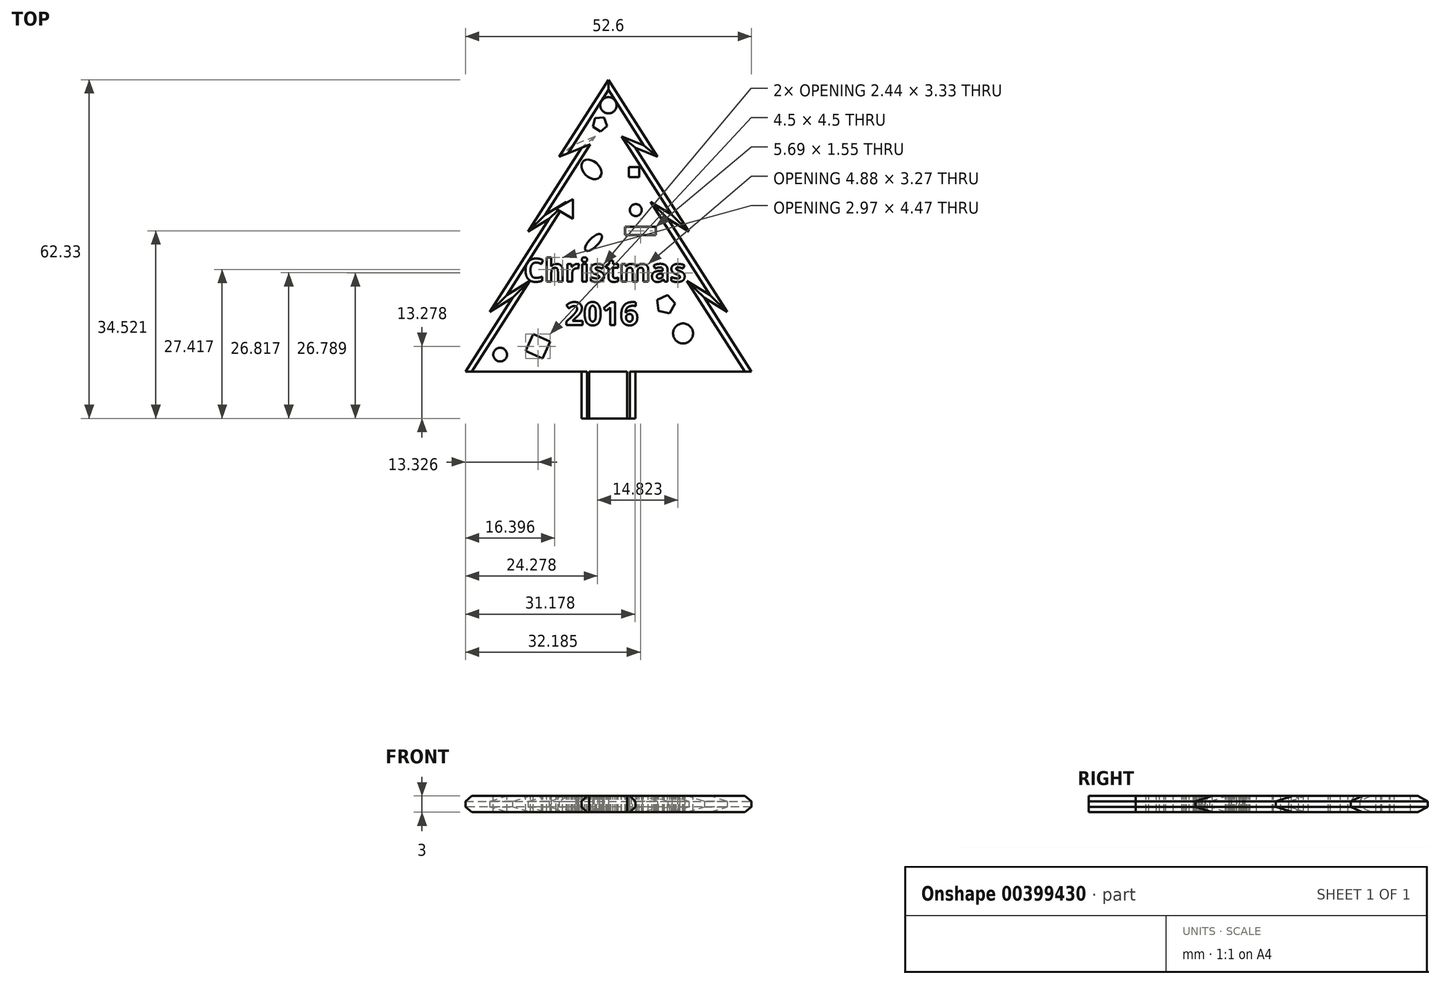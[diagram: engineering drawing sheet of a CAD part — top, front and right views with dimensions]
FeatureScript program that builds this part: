
annotation { "Feature Type Name" : "Feature", "Feature Type Description" : "" }
export const myFeature = defineFeature(function(context is Context, id is Id, definition is map)
    precondition{}
    {
        {
            var Q0;
            Q0=qCreatedBy(makeId("Top.planeOp"),FACE);
            var sketch = newSketch(context, id + "F0", { "sketchPlane" : qUnion([Q0])});
            skLineSegment(sketch, "E0", {"start": v(0, 62.33) * mm, "end": v(-9.05, 48.15) * mm});
            skLineSegment(sketch, "E1", {"start": v(-9.05, 48.15) * mm, "end": v(-4.95, 49.83) * mm});
            skLineSegment(sketch, "E2", {"start": v(-4.95, 49.83) * mm, "end": v(-14.78, 34.42) * mm});
            skLineSegment(sketch, "E3", {"start": v(-14.78, 34.42) * mm, "end": v(-10.92, 36.76) * mm});
            skLineSegment(sketch, "E4", {"start": v(-10.92, 36.76) * mm, "end": v(-21.87, 19.6) * mm});
            skLineSegment(sketch, "E5", {"start": v(-21.87, 19.6) * mm, "end": v(-17.63, 22.2) * mm});
            skLineSegment(sketch, "E6", {"start": v(-17.63, 22.2) * mm, "end": v(-26.3, 8.63) * mm});
            skLineSegment(sketch, "E7", {"start": v(-26.3, 8.63) * mm, "end": v(-4.95, 8.63) * mm});
            skLineSegment(sketch, "E8", {"start": v(-4.95, 8.63) * mm, "end": v(-4.95, 0) * mm});
            skLineSegment(sketch, "E9", {"start": v(-4.95, 0) * mm, "end": v(0, 0) * mm});
            skLineSegment(sketch, "E10.MirrorCS", {"start": v(0, 62.33) * mm, "end": v(9.05, 48.15) * mm});
            skLineSegment(sketch, "E11.MirrorCS", {"start": v(9.05, 48.15) * mm, "end": v(4.95, 49.83) * mm});
            skLineSegment(sketch, "E12.MirrorCS", {"start": v(4.95, 49.83) * mm, "end": v(14.78, 34.42) * mm});
            skLineSegment(sketch, "E13.MirrorCS", {"start": v(14.78, 34.42) * mm, "end": v(10.92, 36.76) * mm});
            skLineSegment(sketch, "E14.MirrorCS", {"start": v(10.92, 36.76) * mm, "end": v(21.87, 19.6) * mm});
            skLineSegment(sketch, "E15.MirrorCS", {"start": v(21.87, 19.6) * mm, "end": v(17.63, 22.2) * mm});
            skLineSegment(sketch, "E16.MirrorCS", {"start": v(17.63, 22.2) * mm, "end": v(26.3, 8.63) * mm});
            skLineSegment(sketch, "E17.MirrorCS", {"start": v(26.3, 8.63) * mm, "end": v(4.95, 8.63) * mm});
            skLineSegment(sketch, "E18.MirrorCS", {"start": v(4.95, 8.63) * mm, "end": v(4.95, 0) * mm});
            skLineSegment(sketch, "E19.MirrorCS", {"start": v(4.95, 0) * mm, "end": v(0, 0) * mm});
            skSolve(sketch);
        }
        {
            var Q0;
            Q0=makeQuery(id+"F0.imprint","IMPRINT",FACE,{"disambiguationData":[TD([[makeQuery(id+"F0.imprint","IMPRINT",EDGE,{"derivedFrom":sQuery(id+"F0.wireOp",EDGE,"E0")}),1.0]])]});
            extrude(context, id + "F1", {"entities" : qUnion([Q0]), "depth" : 3 * mm});
        }
        {
            var Q0;
            Q0=makeQuery(id+"F1.opExtrude","CAP_FACE",FACE,{"disambiguationData":[OSD([sQuery(id+"F0.wireOp",EDGE,"E0"),sQuery(id+"F0.wireOp",EDGE,"E1"),sQuery(id+"F0.wireOp",EDGE,"E2"),sQuery(id+"F0.wireOp",EDGE,"E3"),sQuery(id+"F0.wireOp",EDGE,"E4"),sQuery(id+"F0.wireOp",EDGE,"E5"),sQuery(id+"F0.wireOp",EDGE,"E6"),sQuery(id+"F0.wireOp",EDGE,"E7"),sQuery(id+"F0.wireOp",EDGE,"E8"),sQuery(id+"F0.wireOp",EDGE,"E9"),sQuery(id+"F0.wireOp",EDGE,"E10.MirrorCS"),sQuery(id+"F0.wireOp",EDGE,"E11.MirrorCS"),sQuery(id+"F0.wireOp",EDGE,"E12.MirrorCS"),sQuery(id+"F0.wireOp",EDGE,"E13.MirrorCS"),sQuery(id+"F0.wireOp",EDGE,"E14.MirrorCS"),sQuery(id+"F0.wireOp",EDGE,"E15.MirrorCS"),sQuery(id+"F0.wireOp",EDGE,"E16.MirrorCS"),sQuery(id+"F0.wireOp",EDGE,"E17.MirrorCS"),sQuery(id+"F0.wireOp",EDGE,"E18.MirrorCS"),sQuery(id+"F0.wireOp",EDGE,"E19.MirrorCS")])],"isStart":false});
            var sketch = newSketch(context, id + "F2", { "sketchPlane" : qUnion([Q0])});
            skText(sketch, "E20", { "text": "Christmas\n     2016", "fontName": "OpenSans-Bold.ttf"});
            skCircle(sketch, "E21", {"center": v(13.72, 15.64) * mm, "radius": 1.84 * mm});
            skCircle(sketch, "E22", {"center": v(-19.92, 11.74) * mm, "radius": 1.26 * mm});
            skCircle(sketch, "E23", {"center": v(5.03, 38.35) * mm, "radius": 1.1 * mm});
            skCircle(sketch, "E24.cCircle", {"center": v(-7.57, 38.57) * mm, "radius": 1.05 * mm, "construction": true});
            skLineSegment(sketch, "E24.0", {"start": v(-6.52, 40.4) * mm, "end": v(-6.52, 36.76) * mm});
            skLineSegment(sketch, "E24.1", {"start": v(-6.52, 36.76) * mm, "end": v(-9.67, 38.57) * mm});
            skLineSegment(sketch, "E24.2", {"start": v(-9.67, 38.57) * mm, "end": v(-6.52, 40.4) * mm});
            skPoint(sketch, "E24.0.midPoint", {"position": v(-6.52, 38.57) * mm});
            skCircle(sketch, "E25.cCircle", {"center": v(10.52, 20.96) * mm, "radius": 1.42 * mm, "construction": true});
            skLineSegment(sketch, "E25.0", {"start": v(10.85, 22.69) * mm, "end": v(12.26, 21.18) * mm});
            skLineSegment(sketch, "E25.1", {"start": v(12.26, 21.18) * mm, "end": v(11.27, 19.37) * mm});
            skLineSegment(sketch, "E25.2", {"start": v(11.27, 19.37) * mm, "end": v(9.24, 19.76) * mm});
            skLineSegment(sketch, "E25.3", {"start": v(9.24, 19.76) * mm, "end": v(8.98, 21.8) * mm});
            skLineSegment(sketch, "E25.4", {"start": v(8.98, 21.8) * mm, "end": v(10.85, 22.69) * mm});
            skPoint(sketch, "E25.0.midPoint", {"position": v(11.55, 21.94) * mm});
            skCircle(sketch, "E26.cCircle", {"center": v(-12.97, 13.28) * mm, "radius": 1.7 * mm, "construction": true});
            skLineSegment(sketch, "E26.0", {"start": v(-13.85, 15.53) * mm, "end": v(-10.72, 14.15) * mm});
            skLineSegment(sketch, "E26.1", {"start": v(-10.72, 14.15) * mm, "end": v(-12.1, 11.03) * mm});
            skLineSegment(sketch, "E26.2", {"start": v(-12.1, 11.03) * mm, "end": v(-15.22, 12.4) * mm});
            skLineSegment(sketch, "E26.3", {"start": v(-15.22, 12.4) * mm, "end": v(-13.85, 15.53) * mm});
            skPoint(sketch, "E26.0.midPoint", {"position": v(-12.29, 14.84) * mm});
            skCircle(sketch, "E27.cCircle", {"center": v(-1.57, 54.2) * mm, "radius": 1.13 * mm, "construction": true});
            skLineSegment(sketch, "E27.0", {"start": v(-1.48, 52.8) * mm, "end": v(-2.87, 53.7) * mm});
            skLineSegment(sketch, "E27.1", {"start": v(-2.87, 53.7) * mm, "end": v(-2.46, 55.29) * mm});
            skLineSegment(sketch, "E27.2", {"start": v(-2.46, 55.29) * mm, "end": v(-0.82, 55.39) * mm});
            skLineSegment(sketch, "E27.3", {"start": v(-0.82, 55.39) * mm, "end": v(-0.21, 53.86) * mm});
            skLineSegment(sketch, "E27.4", {"start": v(-0.21, 53.86) * mm, "end": v(-1.48, 52.8) * mm});
            skPoint(sketch, "E27.0.midPoint", {"position": v(-2.18, 53.25) * mm});
            skEllipse(sketch, "E28", {"center": v(-3.13, 45.84) * mm, "majorRadius": 2.12 * mm, "minorRadius": 1.48 * mm, "majorAxis": v(0.74, -0.68)});
            skEllipse(sketch, "E29", {"center": v(-2.74, 32.39) * mm, "majorRadius": 2.05 * mm, "minorRadius": 0.84 * mm, "majorAxis": v(0.7, 0.7)});
            skLineSegment(sketch, "E30.bottom", {"start": v(3.73, 46.27) * mm, "end": v(5.66, 46.27) * mm});
            skLineSegment(sketch, "E30.top", {"start": v(3.73, 44.42) * mm, "end": v(5.66, 44.42) * mm});
            skLineSegment(sketch, "E30.left", {"start": v(3.73, 46.27) * mm, "end": v(3.73, 44.42) * mm});
            skLineSegment(sketch, "E30.right", {"start": v(5.66, 46.27) * mm, "end": v(5.66, 44.42) * mm});
            skLineSegment(sketch, "E31.bottom", {"start": v(3.04, 35.3) * mm, "end": v(8.73, 35.3) * mm});
            skLineSegment(sketch, "E31.top", {"start": v(3.04, 33.74) * mm, "end": v(8.73, 33.74) * mm});
            skLineSegment(sketch, "E31.left", {"start": v(3.04, 35.3) * mm, "end": v(3.04, 33.74) * mm});
            skLineSegment(sketch, "E31.right", {"start": v(8.73, 35.3) * mm, "end": v(8.73, 33.74) * mm});
            skLineSegment(sketch, "E32.bottom", {"start": v(-3.57, 8.63) * mm, "end": v(3.4, 8.63) * mm});
            skLineSegment(sketch, "E32.top", {"start": v(-3.57, 0) * mm, "end": v(3.4, 0) * mm});
            skLineSegment(sketch, "E32.left", {"start": v(-3.57, 8.63) * mm, "end": v(-3.57, 0) * mm});
            skLineSegment(sketch, "E32.right", {"start": v(3.4, 8.63) * mm, "end": v(3.4, 0) * mm});
            const initialGuessF2  = {"E20": [-0.0156, 0.02518, 1, 0, 0.00424]};
            skSetInitialGuess(sketch, initialGuessF2);
            skSolve(sketch);
        }
        {
            var Q0;
            Q0 = qSketchRegion(id + "F2", true);
            extrude(context, id + "F3", {"entities" : qUnion([Q0]), "depth" : 0 * mm, "hasSecondDirection" : true, "secondDirectionOppositeDirection" : true, "secondDirectionDepth" : 3 * mm});
        }
        {
            var Q0;
            Q0=makeQuery(id+"F3.opExtrude","SWEPT_BODY",BODY,{"disambiguationData":[OSD([sQuery(id+"F2.wireOp",EDGE,"E20.sketch_text.stroke-50"),sQuery(id+"F2.wireOp",EDGE,"E20.sketch_text.stroke-51"),sQuery(id+"F2.wireOp",EDGE,"E20.sketch_text.stroke-52"),sQuery(id+"F2.wireOp",EDGE,"E20.sketch_text.stroke-53")])]});
            var Q1;
            Q1=makeQuery(id+"F3.opExtrude","SWEPT_BODY",BODY,{"disambiguationData":[OSD([sQuery(id+"F2.wireOp",EDGE,"E29")])]});
            var Q2;
            Q2=makeQuery(id+"F3.opExtrude","SWEPT_BODY",BODY,{"disambiguationData":[OSD([sQuery(id+"F2.wireOp",EDGE,"E20.sketch_text.stroke-15"),sQuery(id+"F2.wireOp",EDGE,"E20.sketch_text.stroke-16"),sQuery(id+"F2.wireOp",EDGE,"E20.sketch_text.stroke-17"),sQuery(id+"F2.wireOp",EDGE,"E20.sketch_text.stroke-18"),sQuery(id+"F2.wireOp",EDGE,"E20.sketch_text.stroke-19"),sQuery(id+"F2.wireOp",EDGE,"E20.sketch_text.stroke-20"),sQuery(id+"F2.wireOp",EDGE,"E20.sketch_text.stroke-21"),sQuery(id+"F2.wireOp",EDGE,"E20.sketch_text.stroke-22"),sQuery(id+"F2.wireOp",EDGE,"E20.sketch_text.stroke-23"),sQuery(id+"F2.wireOp",EDGE,"E20.sketch_text.stroke-24"),sQuery(id+"F2.wireOp",EDGE,"E20.sketch_text.stroke-25"),sQuery(id+"F2.wireOp",EDGE,"E20.sketch_text.stroke-26"),sQuery(id+"F2.wireOp",EDGE,"E20.sketch_text.stroke-27"),sQuery(id+"F2.wireOp",EDGE,"E20.sketch_text.stroke-28"),sQuery(id+"F2.wireOp",EDGE,"E20.sketch_text.stroke-29"),sQuery(id+"F2.wireOp",EDGE,"E20.sketch_text.stroke-30"),sQuery(id+"F2.wireOp",EDGE,"E20.sketch_text.stroke-31")])]});
            var Q3;
            Q3=makeQuery(id+"F3.opExtrude","SWEPT_BODY",BODY,{"disambiguationData":[OSD([sQuery(id+"F2.wireOp",EDGE,"E20.sketch_text.stroke-32"),sQuery(id+"F2.wireOp",EDGE,"E20.sketch_text.stroke-33"),sQuery(id+"F2.wireOp",EDGE,"E20.sketch_text.stroke-34"),sQuery(id+"F2.wireOp",EDGE,"E20.sketch_text.stroke-35"),sQuery(id+"F2.wireOp",EDGE,"E20.sketch_text.stroke-36"),sQuery(id+"F2.wireOp",EDGE,"E20.sketch_text.stroke-37"),sQuery(id+"F2.wireOp",EDGE,"E20.sketch_text.stroke-38"),sQuery(id+"F2.wireOp",EDGE,"E20.sketch_text.stroke-39"),sQuery(id+"F2.wireOp",EDGE,"E20.sketch_text.stroke-40"),sQuery(id+"F2.wireOp",EDGE,"E20.sketch_text.stroke-41"),sQuery(id+"F2.wireOp",EDGE,"E20.sketch_text.stroke-42"),sQuery(id+"F2.wireOp",EDGE,"E20.sketch_text.stroke-43"),sQuery(id+"F2.wireOp",EDGE,"E20.sketch_text.stroke-44")])]});
            var Q4;
            Q4=makeQuery(id+"F3.opExtrude","SWEPT_BODY",BODY,{"disambiguationData":[OSD([sQuery(id+"F2.wireOp",EDGE,"E20.sketch_text.stroke-45"),sQuery(id+"F2.wireOp",EDGE,"E20.sketch_text.stroke-46"),sQuery(id+"F2.wireOp",EDGE,"E20.sketch_text.stroke-47"),sQuery(id+"F2.wireOp",EDGE,"E20.sketch_text.stroke-48"),sQuery(id+"F2.wireOp",EDGE,"E20.sketch_text.stroke-49")])]});
            var Q5;
            Q5=makeQuery(id+"F3.opExtrude","SWEPT_BODY",BODY,{"disambiguationData":[OSD([sQuery(id+"F2.wireOp",EDGE,"E20.sketch_text.stroke-54"),sQuery(id+"F2.wireOp",EDGE,"E20.sketch_text.stroke-55"),sQuery(id+"F2.wireOp",EDGE,"E20.sketch_text.stroke-56"),sQuery(id+"F2.wireOp",EDGE,"E20.sketch_text.stroke-57"),sQuery(id+"F2.wireOp",EDGE,"E20.sketch_text.stroke-58"),sQuery(id+"F2.wireOp",EDGE,"E20.sketch_text.stroke-59"),sQuery(id+"F2.wireOp",EDGE,"E20.sketch_text.stroke-60"),sQuery(id+"F2.wireOp",EDGE,"E20.sketch_text.stroke-61"),sQuery(id+"F2.wireOp",EDGE,"E20.sketch_text.stroke-62"),sQuery(id+"F2.wireOp",EDGE,"E20.sketch_text.stroke-63"),sQuery(id+"F2.wireOp",EDGE,"E20.sketch_text.stroke-64"),sQuery(id+"F2.wireOp",EDGE,"E20.sketch_text.stroke-65"),sQuery(id+"F2.wireOp",EDGE,"E20.sketch_text.stroke-66"),sQuery(id+"F2.wireOp",EDGE,"E20.sketch_text.stroke-67"),sQuery(id+"F2.wireOp",EDGE,"E20.sketch_text.stroke-68"),sQuery(id+"F2.wireOp",EDGE,"E20.sketch_text.stroke-69"),sQuery(id+"F2.wireOp",EDGE,"E20.sketch_text.stroke-70"),sQuery(id+"F2.wireOp",EDGE,"E20.sketch_text.stroke-71"),sQuery(id+"F2.wireOp",EDGE,"E20.sketch_text.stroke-72"),sQuery(id+"F2.wireOp",EDGE,"E20.sketch_text.stroke-73"),sQuery(id+"F2.wireOp",EDGE,"E20.sketch_text.stroke-74"),sQuery(id+"F2.wireOp",EDGE,"E20.sketch_text.stroke-75"),sQuery(id+"F2.wireOp",EDGE,"E20.sketch_text.stroke-76"),sQuery(id+"F2.wireOp",EDGE,"E20.sketch_text.stroke-77"),sQuery(id+"F2.wireOp",EDGE,"E20.sketch_text.stroke-78"),sQuery(id+"F2.wireOp",EDGE,"E20.sketch_text.stroke-79")])]});
            var Q6;
            Q6=makeQuery(id+"F3.opExtrude","SWEPT_BODY",BODY,{"disambiguationData":[OSD([sQuery(id+"F2.wireOp",EDGE,"E20.sketch_text.stroke-80"),sQuery(id+"F2.wireOp",EDGE,"E20.sketch_text.stroke-81"),sQuery(id+"F2.wireOp",EDGE,"E20.sketch_text.stroke-82"),sQuery(id+"F2.wireOp",EDGE,"E20.sketch_text.stroke-83"),sQuery(id+"F2.wireOp",EDGE,"E20.sketch_text.stroke-84"),sQuery(id+"F2.wireOp",EDGE,"E20.sketch_text.stroke-85"),sQuery(id+"F2.wireOp",EDGE,"E20.sketch_text.stroke-86"),sQuery(id+"F2.wireOp",EDGE,"E20.sketch_text.stroke-87"),sQuery(id+"F2.wireOp",EDGE,"E20.sketch_text.stroke-88"),sQuery(id+"F2.wireOp",EDGE,"E20.sketch_text.stroke-89"),sQuery(id+"F2.wireOp",EDGE,"E20.sketch_text.stroke-90"),sQuery(id+"F2.wireOp",EDGE,"E20.sketch_text.stroke-91"),sQuery(id+"F2.wireOp",EDGE,"E20.sketch_text.stroke-92"),sQuery(id+"F2.wireOp",EDGE,"E20.sketch_text.stroke-93"),sQuery(id+"F2.wireOp",EDGE,"E20.sketch_text.stroke-94"),sQuery(id+"F2.wireOp",EDGE,"E20.sketch_text.stroke-95"),sQuery(id+"F2.wireOp",EDGE,"E20.sketch_text.stroke-96"),sQuery(id+"F2.wireOp",EDGE,"E20.sketch_text.stroke-97")])]});
            var Q7;
            Q7=makeQuery(id+"F3.opExtrude","SWEPT_BODY",BODY,{"disambiguationData":[OSD([sQuery(id+"F2.wireOp",EDGE,"E20.sketch_text.stroke-98"),sQuery(id+"F2.wireOp",EDGE,"E20.sketch_text.stroke-99"),sQuery(id+"F2.wireOp",EDGE,"E20.sketch_text.stroke-100"),sQuery(id+"F2.wireOp",EDGE,"E20.sketch_text.stroke-101"),sQuery(id+"F2.wireOp",EDGE,"E20.sketch_text.stroke-102"),sQuery(id+"F2.wireOp",EDGE,"E20.sketch_text.stroke-103"),sQuery(id+"F2.wireOp",EDGE,"E20.sketch_text.stroke-104"),sQuery(id+"F2.wireOp",EDGE,"E20.sketch_text.stroke-105"),sQuery(id+"F2.wireOp",EDGE,"E20.sketch_text.stroke-106"),sQuery(id+"F2.wireOp",EDGE,"E20.sketch_text.stroke-107"),sQuery(id+"F2.wireOp",EDGE,"E20.sketch_text.stroke-108"),sQuery(id+"F2.wireOp",EDGE,"E20.sketch_text.stroke-109"),sQuery(id+"F2.wireOp",EDGE,"E20.sketch_text.stroke-110"),sQuery(id+"F2.wireOp",EDGE,"E20.sketch_text.stroke-111"),sQuery(id+"F2.wireOp",EDGE,"E20.sketch_text.stroke-112"),sQuery(id+"F2.wireOp",EDGE,"E20.sketch_text.stroke-113"),sQuery(id+"F2.wireOp",EDGE,"E20.sketch_text.stroke-114"),sQuery(id+"F2.wireOp",EDGE,"E20.sketch_text.stroke-115"),sQuery(id+"F2.wireOp",EDGE,"E20.sketch_text.stroke-116"),sQuery(id+"F2.wireOp",EDGE,"E20.sketch_text.stroke-117"),sQuery(id+"F2.wireOp",EDGE,"E20.sketch_text.stroke-118"),sQuery(id+"F2.wireOp",EDGE,"E20.sketch_text.stroke-119"),sQuery(id+"F2.wireOp",EDGE,"E20.sketch_text.stroke-120"),sQuery(id+"F2.wireOp",EDGE,"E20.sketch_text.stroke-121"),sQuery(id+"F2.wireOp",EDGE,"E20.sketch_text.stroke-122"),sQuery(id+"F2.wireOp",EDGE,"E20.sketch_text.stroke-123"),sQuery(id+"F2.wireOp",EDGE,"E20.sketch_text.stroke-124"),sQuery(id+"F2.wireOp",EDGE,"E20.sketch_text.stroke-125")])]});
            var Q8;
            Q8=makeQuery(id+"F3.opExtrude","SWEPT_BODY",BODY,{"disambiguationData":[OSD([sQuery(id+"F2.wireOp",EDGE,"E20.sketch_text.stroke-126"),sQuery(id+"F2.wireOp",EDGE,"E20.sketch_text.stroke-127"),sQuery(id+"F2.wireOp",EDGE,"E20.sketch_text.stroke-128"),sQuery(id+"F2.wireOp",EDGE,"E20.sketch_text.stroke-129"),sQuery(id+"F2.wireOp",EDGE,"E20.sketch_text.stroke-130"),sQuery(id+"F2.wireOp",EDGE,"E20.sketch_text.stroke-131"),sQuery(id+"F2.wireOp",EDGE,"E20.sketch_text.stroke-132"),sQuery(id+"F2.wireOp",EDGE,"E20.sketch_text.stroke-133"),sQuery(id+"F2.wireOp",EDGE,"E20.sketch_text.stroke-134"),sQuery(id+"F2.wireOp",EDGE,"E20.sketch_text.stroke-135"),sQuery(id+"F2.wireOp",EDGE,"E20.sketch_text.stroke-136"),sQuery(id+"F2.wireOp",EDGE,"E20.sketch_text.stroke-137"),sQuery(id+"F2.wireOp",EDGE,"E20.sketch_text.stroke-138"),sQuery(id+"F2.wireOp",EDGE,"E20.sketch_text.stroke-139"),sQuery(id+"F2.wireOp",EDGE,"E20.sketch_text.stroke-140"),sQuery(id+"F2.wireOp",EDGE,"E20.sketch_text.stroke-141"),sQuery(id+"F2.wireOp",EDGE,"E20.sketch_text.stroke-142"),sQuery(id+"F2.wireOp",EDGE,"E20.sketch_text.stroke-143"),sQuery(id+"F2.wireOp",EDGE,"E20.sketch_text.stroke-144"),sQuery(id+"F2.wireOp",EDGE,"E20.sketch_text.stroke-145"),sQuery(id+"F2.wireOp",EDGE,"E20.sketch_text.stroke-146"),sQuery(id+"F2.wireOp",EDGE,"E20.sketch_text.stroke-147"),sQuery(id+"F2.wireOp",EDGE,"E20.sketch_text.stroke-148"),sQuery(id+"F2.wireOp",EDGE,"E20.sketch_text.stroke-149"),sQuery(id+"F2.wireOp",EDGE,"E20.sketch_text.stroke-150")])]});
            var Q9;
            Q9=makeQuery(id+"F3.opExtrude","SWEPT_BODY",BODY,{"disambiguationData":[OSD([sQuery(id+"F2.wireOp",EDGE,"E20.sketch_text.stroke-151"),sQuery(id+"F2.wireOp",EDGE,"E20.sketch_text.stroke-152"),sQuery(id+"F2.wireOp",EDGE,"E20.sketch_text.stroke-153"),sQuery(id+"F2.wireOp",EDGE,"E20.sketch_text.stroke-154"),sQuery(id+"F2.wireOp",EDGE,"E20.sketch_text.stroke-155"),sQuery(id+"F2.wireOp",EDGE,"E20.sketch_text.stroke-156"),sQuery(id+"F2.wireOp",EDGE,"E20.sketch_text.stroke-157"),sQuery(id+"F2.wireOp",EDGE,"E20.sketch_text.stroke-158"),sQuery(id+"F2.wireOp",EDGE,"E20.sketch_text.stroke-159"),sQuery(id+"F2.wireOp",EDGE,"E20.sketch_text.stroke-160"),sQuery(id+"F2.wireOp",EDGE,"E20.sketch_text.stroke-161"),sQuery(id+"F2.wireOp",EDGE,"E20.sketch_text.stroke-162"),sQuery(id+"F2.wireOp",EDGE,"E20.sketch_text.stroke-163"),sQuery(id+"F2.wireOp",EDGE,"E20.sketch_text.stroke-164"),sQuery(id+"F2.wireOp",EDGE,"E20.sketch_text.stroke-165"),sQuery(id+"F2.wireOp",EDGE,"E20.sketch_text.stroke-166"),sQuery(id+"F2.wireOp",EDGE,"E20.sketch_text.stroke-167"),sQuery(id+"F2.wireOp",EDGE,"E20.sketch_text.stroke-168"),sQuery(id+"F2.wireOp",EDGE,"E20.sketch_text.stroke-169"),sQuery(id+"F2.wireOp",EDGE,"E20.sketch_text.stroke-170"),sQuery(id+"F2.wireOp",EDGE,"E20.sketch_text.stroke-171"),sQuery(id+"F2.wireOp",EDGE,"E20.sketch_text.stroke-172"),sQuery(id+"F2.wireOp",EDGE,"E20.sketch_text.stroke-173"),sQuery(id+"F2.wireOp",EDGE,"E20.sketch_text.stroke-174"),sQuery(id+"F2.wireOp",EDGE,"E20.sketch_text.stroke-175"),sQuery(id+"F2.wireOp",EDGE,"E20.sketch_text.stroke-176")])]});
            var Q10;
            Q10=makeQuery(id+"F3.opExtrude","SWEPT_BODY",BODY,{"disambiguationData":[OSD([sQuery(id+"F2.wireOp",EDGE,"E20.sketch_text.stroke-177"),sQuery(id+"F2.wireOp",EDGE,"E20.sketch_text.stroke-178"),sQuery(id+"F2.wireOp",EDGE,"E20.sketch_text.stroke-179"),sQuery(id+"F2.wireOp",EDGE,"E20.sketch_text.stroke-180"),sQuery(id+"F2.wireOp",EDGE,"E20.sketch_text.stroke-181"),sQuery(id+"F2.wireOp",EDGE,"E20.sketch_text.stroke-182"),sQuery(id+"F2.wireOp",EDGE,"E20.sketch_text.stroke-183"),sQuery(id+"F2.wireOp",EDGE,"E20.sketch_text.stroke-184"),sQuery(id+"F2.wireOp",EDGE,"E20.sketch_text.stroke-185"),sQuery(id+"F2.wireOp",EDGE,"E20.sketch_text.stroke-186"),sQuery(id+"F2.wireOp",EDGE,"E20.sketch_text.stroke-187"),sQuery(id+"F2.wireOp",EDGE,"E20.sketch_text.stroke-188"),sQuery(id+"F2.wireOp",EDGE,"E20.sketch_text.stroke-189"),sQuery(id+"F2.wireOp",EDGE,"E20.sketch_text.stroke-190"),sQuery(id+"F2.wireOp",EDGE,"E20.sketch_text.stroke-191"),sQuery(id+"F2.wireOp",EDGE,"E20.sketch_text.stroke-192"),sQuery(id+"F2.wireOp",EDGE,"E20.sketch_text.stroke-193"),sQuery(id+"F2.wireOp",EDGE,"E20.sketch_text.stroke-194"),sQuery(id+"F2.wireOp",EDGE,"E20.sketch_text.stroke-195"),sQuery(id+"F2.wireOp",EDGE,"E20.sketch_text.stroke-196"),sQuery(id+"F2.wireOp",EDGE,"E20.sketch_text.stroke-197"),sQuery(id+"F2.wireOp",EDGE,"E20.sketch_text.stroke-198"),sQuery(id+"F2.wireOp",EDGE,"E20.sketch_text.stroke-199"),sQuery(id+"F2.wireOp",EDGE,"E20.sketch_text.stroke-200")])]});
            var Q11;
            Q11=makeQuery(id+"F3.opExtrude","SWEPT_BODY",BODY,{"disambiguationData":[OSD([sQuery(id+"F2.wireOp",EDGE,"E20.sketch_text.stroke-201"),sQuery(id+"F2.wireOp",EDGE,"E20.sketch_text.stroke-202"),sQuery(id+"F2.wireOp",EDGE,"E20.sketch_text.stroke-203"),sQuery(id+"F2.wireOp",EDGE,"E20.sketch_text.stroke-204"),sQuery(id+"F2.wireOp",EDGE,"E20.sketch_text.stroke-205"),sQuery(id+"F2.wireOp",EDGE,"E20.sketch_text.stroke-206"),sQuery(id+"F2.wireOp",EDGE,"E20.sketch_text.stroke-207"),sQuery(id+"F2.wireOp",EDGE,"E20.sketch_text.stroke-208"),sQuery(id+"F2.wireOp",EDGE,"E20.sketch_text.stroke-209"),sQuery(id+"F2.wireOp",EDGE,"E20.sketch_text.stroke-210"),sQuery(id+"F2.wireOp",EDGE,"E20.sketch_text.stroke-211"),sQuery(id+"F2.wireOp",EDGE,"E20.sketch_text.stroke-212"),sQuery(id+"F2.wireOp",EDGE,"E20.sketch_text.stroke-213"),sQuery(id+"F2.wireOp",EDGE,"E20.sketch_text.stroke-214"),sQuery(id+"F2.wireOp",EDGE,"E20.sketch_text.stroke-215"),sQuery(id+"F2.wireOp",EDGE,"E20.sketch_text.stroke-216")])]});
            var Q12;
            Q12=makeQuery(id+"F3.opExtrude","SWEPT_BODY",BODY,{"disambiguationData":[OSD([sQuery(id+"F2.wireOp",EDGE,"E20.sketch_text.stroke-217"),sQuery(id+"F2.wireOp",EDGE,"E20.sketch_text.stroke-218"),sQuery(id+"F2.wireOp",EDGE,"E20.sketch_text.stroke-219"),sQuery(id+"F2.wireOp",EDGE,"E20.sketch_text.stroke-220"),sQuery(id+"F2.wireOp",EDGE,"E20.sketch_text.stroke-221"),sQuery(id+"F2.wireOp",EDGE,"E20.sketch_text.stroke-222"),sQuery(id+"F2.wireOp",EDGE,"E20.sketch_text.stroke-223"),sQuery(id+"F2.wireOp",EDGE,"E20.sketch_text.stroke-224"),sQuery(id+"F2.wireOp",EDGE,"E20.sketch_text.stroke-225"),sQuery(id+"F2.wireOp",EDGE,"E20.sketch_text.stroke-226")])]});
            var Q13;
            Q13=makeQuery(id+"F3.opExtrude","SWEPT_BODY",BODY,{"disambiguationData":[OSD([sQuery(id+"F2.wireOp",EDGE,"E20.sketch_text.stroke-227"),sQuery(id+"F2.wireOp",EDGE,"E20.sketch_text.stroke-228"),sQuery(id+"F2.wireOp",EDGE,"E20.sketch_text.stroke-229"),sQuery(id+"F2.wireOp",EDGE,"E20.sketch_text.stroke-230"),sQuery(id+"F2.wireOp",EDGE,"E20.sketch_text.stroke-231"),sQuery(id+"F2.wireOp",EDGE,"E20.sketch_text.stroke-232"),sQuery(id+"F2.wireOp",EDGE,"E20.sketch_text.stroke-233"),sQuery(id+"F2.wireOp",EDGE,"E20.sketch_text.stroke-234"),sQuery(id+"F2.wireOp",EDGE,"E20.sketch_text.stroke-235"),sQuery(id+"F2.wireOp",EDGE,"E20.sketch_text.stroke-236"),sQuery(id+"F2.wireOp",EDGE,"E20.sketch_text.stroke-237"),sQuery(id+"F2.wireOp",EDGE,"E20.sketch_text.stroke-238"),sQuery(id+"F2.wireOp",EDGE,"E20.sketch_text.stroke-239"),sQuery(id+"F2.wireOp",EDGE,"E20.sketch_text.stroke-240"),sQuery(id+"F2.wireOp",EDGE,"E20.sketch_text.stroke-241"),sQuery(id+"F2.wireOp",EDGE,"E20.sketch_text.stroke-242"),sQuery(id+"F2.wireOp",EDGE,"E20.sketch_text.stroke-243"),sQuery(id+"F2.wireOp",EDGE,"E20.sketch_text.stroke-244"),sQuery(id+"F2.wireOp",EDGE,"E20.sketch_text.stroke-245"),sQuery(id+"F2.wireOp",EDGE,"E20.sketch_text.stroke-246"),sQuery(id+"F2.wireOp",EDGE,"E20.sketch_text.stroke-247"),sQuery(id+"F2.wireOp",EDGE,"E20.sketch_text.stroke-248"),sQuery(id+"F2.wireOp",EDGE,"E20.sketch_text.stroke-249"),sQuery(id+"F2.wireOp",EDGE,"E20.sketch_text.stroke-250"),sQuery(id+"F2.wireOp",EDGE,"E20.sketch_text.stroke-251")])]});
            var Q14;
            Q14=makeQuery(id+"F3.opExtrude","SWEPT_BODY",BODY,{"disambiguationData":[OSD([sQuery(id+"F2.wireOp",EDGE,"E21")])]});
            var Q15;
            Q15=makeQuery(id+"F3.opExtrude","SWEPT_BODY",BODY,{"disambiguationData":[OSD([sQuery(id+"F2.wireOp",EDGE,"E23")])]});
            var Q16;
            Q16=makeQuery(id+"F3.opExtrude","SWEPT_BODY",BODY,{"disambiguationData":[OSD([sQuery(id+"F2.wireOp",EDGE,"E24.0"),sQuery(id+"F2.wireOp",EDGE,"E24.1"),sQuery(id+"F2.wireOp",EDGE,"E24.2")])]});
            var Q17;
            Q17=makeQuery(id+"F3.opExtrude","SWEPT_BODY",BODY,{"disambiguationData":[OSD([sQuery(id+"F2.wireOp",EDGE,"E25.0"),sQuery(id+"F2.wireOp",EDGE,"E25.1"),sQuery(id+"F2.wireOp",EDGE,"E25.2"),sQuery(id+"F2.wireOp",EDGE,"E25.3"),sQuery(id+"F2.wireOp",EDGE,"E25.4")])]});
            var Q18;
            Q18=makeQuery(id+"F3.opExtrude","SWEPT_BODY",BODY,{"disambiguationData":[OSD([sQuery(id+"F2.wireOp",EDGE,"E26.0"),sQuery(id+"F2.wireOp",EDGE,"E26.1"),sQuery(id+"F2.wireOp",EDGE,"E26.2"),sQuery(id+"F2.wireOp",EDGE,"E26.3")])]});
            var Q19;
            Q19=makeQuery(id+"F3.opExtrude","SWEPT_BODY",BODY,{"disambiguationData":[OSD([sQuery(id+"F2.wireOp",EDGE,"E27.0"),sQuery(id+"F2.wireOp",EDGE,"E27.1"),sQuery(id+"F2.wireOp",EDGE,"E27.2"),sQuery(id+"F2.wireOp",EDGE,"E27.3"),sQuery(id+"F2.wireOp",EDGE,"E27.4")])]});
            var Q20;
            Q20=makeQuery(id+"F3.opExtrude","SWEPT_BODY",BODY,{"disambiguationData":[OSD([sQuery(id+"F2.wireOp",EDGE,"E28")])]});
            var Q21;
            Q21=makeQuery(id+"F3.opExtrude","SWEPT_BODY",BODY,{"disambiguationData":[OSD([sQuery(id+"F2.wireOp",EDGE,"E30.bottom"),sQuery(id+"F2.wireOp",EDGE,"E30.top"),sQuery(id+"F2.wireOp",EDGE,"E30.left"),sQuery(id+"F2.wireOp",EDGE,"E30.right")])]});
            var Q22;
            Q22=makeQuery(id+"F3.opExtrude","SWEPT_BODY",BODY,{"disambiguationData":[OSD([sQuery(id+"F2.wireOp",EDGE,"E31.bottom"),sQuery(id+"F2.wireOp",EDGE,"E31.top"),sQuery(id+"F2.wireOp",EDGE,"E31.left"),sQuery(id+"F2.wireOp",EDGE,"E31.right")])]});
            var Q23;
            Q23=makeQuery(id+"F3.opExtrude","SWEPT_BODY",BODY,{"disambiguationData":[OSD([sQuery(id+"F2.wireOp",EDGE,"E22")])]});
            var Q24;
            Q24=makeQuery(id+"F3.opExtrude","SWEPT_BODY",BODY,{"disambiguationData":[OSD([sQuery(id+"F2.wireOp",EDGE,"E32.bottom"),sQuery(id+"F2.wireOp",EDGE,"E32.top"),sQuery(id+"F2.wireOp",EDGE,"E32.left"),sQuery(id+"F2.wireOp",EDGE,"E32.right")])]});
            var Q25;
            Q25=makeQuery(id+"F3.opExtrude","SWEPT_BODY",BODY,{"disambiguationData":[OSD([sQuery(id+"F2.wireOp",EDGE,"E20.sketch_text.stroke-0"),sQuery(id+"F2.wireOp",EDGE,"E20.sketch_text.stroke-1"),sQuery(id+"F2.wireOp",EDGE,"E20.sketch_text.stroke-2"),sQuery(id+"F2.wireOp",EDGE,"E20.sketch_text.stroke-3"),sQuery(id+"F2.wireOp",EDGE,"E20.sketch_text.stroke-4"),sQuery(id+"F2.wireOp",EDGE,"E20.sketch_text.stroke-5"),sQuery(id+"F2.wireOp",EDGE,"E20.sketch_text.stroke-6"),sQuery(id+"F2.wireOp",EDGE,"E20.sketch_text.stroke-7"),sQuery(id+"F2.wireOp",EDGE,"E20.sketch_text.stroke-8"),sQuery(id+"F2.wireOp",EDGE,"E20.sketch_text.stroke-9"),sQuery(id+"F2.wireOp",EDGE,"E20.sketch_text.stroke-10"),sQuery(id+"F2.wireOp",EDGE,"E20.sketch_text.stroke-11"),sQuery(id+"F2.wireOp",EDGE,"E20.sketch_text.stroke-12"),sQuery(id+"F2.wireOp",EDGE,"E20.sketch_text.stroke-13"),sQuery(id+"F2.wireOp",EDGE,"E20.sketch_text.stroke-14")])]});
            var Q26;
            Q26=makeQuery(id+"F1.opExtrude","SWEPT_BODY",BODY,{"disambiguationData":[OSD([sQuery(id+"F0.wireOp",EDGE,"E0"),sQuery(id+"F0.wireOp",EDGE,"E1"),sQuery(id+"F0.wireOp",EDGE,"E2"),sQuery(id+"F0.wireOp",EDGE,"E3"),sQuery(id+"F0.wireOp",EDGE,"E4"),sQuery(id+"F0.wireOp",EDGE,"E5"),sQuery(id+"F0.wireOp",EDGE,"E6"),sQuery(id+"F0.wireOp",EDGE,"E7"),sQuery(id+"F0.wireOp",EDGE,"E8"),sQuery(id+"F0.wireOp",EDGE,"E9"),sQuery(id+"F0.wireOp",EDGE,"E10.MirrorCS"),sQuery(id+"F0.wireOp",EDGE,"E11.MirrorCS"),sQuery(id+"F0.wireOp",EDGE,"E12.MirrorCS"),sQuery(id+"F0.wireOp",EDGE,"E13.MirrorCS"),sQuery(id+"F0.wireOp",EDGE,"E14.MirrorCS"),sQuery(id+"F0.wireOp",EDGE,"E15.MirrorCS"),sQuery(id+"F0.wireOp",EDGE,"E16.MirrorCS"),sQuery(id+"F0.wireOp",EDGE,"E17.MirrorCS"),sQuery(id+"F0.wireOp",EDGE,"E18.MirrorCS"),sQuery(id+"F0.wireOp",EDGE,"E19.MirrorCS")])]});
            booleanBodies(context, id + "F4", {"operationType" : BooleanOperationType.SUBTRACTION, "tools" : qUnion([Q0, Q1, Q2, Q3, Q4, Q5, Q6, Q7, Q8, Q9, Q10, Q11, Q12, Q13, Q14, Q15, Q16, Q17, Q18, Q19, Q20, Q21, Q22, Q23, Q24, Q25]), "targets" : qUnion([Q26]), "keepTools" : true});
        }
        {
            var Q0;
            {var subQ0=sQuery(id+"F0.wireOp",EDGE,"E8");var subQ1=sQuery(id+"F0.wireOp",EDGE,"E7");var subQ2=sQuery(id+"F0.wireOp",EDGE,"E6");var subQ3=sQuery(id+"F0.wireOp",EDGE,"E5");var subQ4=sQuery(id+"F0.wireOp",EDGE,"E4");var subQ5=sQuery(id+"F0.wireOp",EDGE,"E19.MirrorCS");var subQ6=sQuery(id+"F0.wireOp",EDGE,"E9");var subQ7=sQuery(id+"F0.wireOp",EDGE,"E0");var subQ8=sQuery(id+"F0.wireOp",EDGE,"E3");var subQ9=sQuery(id+"F0.wireOp",EDGE,"E1");var subQ10=sQuery(id+"F0.wireOp",EDGE,"E2");var subQ11=sQuery(id+"F0.wireOp",EDGE,"E16.MirrorCS");var subQ12=sQuery(id+"F0.wireOp",EDGE,"E10.MirrorCS");var subQ13=sQuery(id+"F0.wireOp",EDGE,"E11.MirrorCS");var subQ14=sQuery(id+"F0.wireOp",EDGE,"E12.MirrorCS");var subQ15=sQuery(id+"F0.wireOp",EDGE,"E13.MirrorCS");var subQ16=sQuery(id+"F0.wireOp",EDGE,"E14.MirrorCS");var subQ17=sQuery(id+"F0.wireOp",EDGE,"E15.MirrorCS");var subQ18=sQuery(id+"F0.wireOp",EDGE,"E17.MirrorCS");var subQ19=sQuery(id+"F0.wireOp",EDGE,"E18.MirrorCS");Q0=makeQuery(id+"F4.opBoolean","SPLIT",FACE,{"disambiguationData":[TD([makeQuery(id+"F1.opExtrude","SWEPT_FACE",FACE,{"disambiguationData":[OSD([subQ7])]})])],"derivedFrom":makeQuery(id+"F1.opExtrude","CAP_FACE",FACE,{"disambiguationData":[OSD([subQ7,subQ9,subQ10,subQ8,subQ4,subQ3,subQ2,subQ1,subQ0,subQ6,subQ12,subQ13,subQ14,subQ15,subQ16,subQ17,subQ11,subQ18,subQ19,subQ5])],"isStart":false})});}
            var sketch = newSketch(context, id + "F5", { "sketchPlane" : qUnion([Q0])});
            skCircle(sketch, "E33", {"center": v(0, 57.65) * mm, "radius": 1.5 * mm});
            skSolve(sketch);
        }
        {
            var Q0;
            Q0=makeQuery(id+"F5.imprint","IMPRINT",FACE,{"disambiguationData":[TD([[makeQuery(id+"F5.imprint","IMPRINT",EDGE,{"derivedFrom":sQuery(id+"F5.wireOp",EDGE,"E33")}),1.0]])]});
            extrude(context, id + "F6", {"entities" : qUnion([Q0]), "operationType" : NewBodyOperationType.REMOVE, "oppositeDirection" : true, "depth" : 25 * mm});
        }
        {
            var Q0;
            Q0=makeQuery(id+"F1.opExtrude","CAP_EDGE",EDGE,{"disambiguationData":[OSD([sQuery(id+"F0.wireOp",EDGE,"E0")])],"isStart":false});
            var Q1;
            Q1=makeQuery(id+"F1.opExtrude","CAP_EDGE",EDGE,{"disambiguationData":[OSD([sQuery(id+"F0.wireOp",EDGE,"E10.MirrorCS")])],"isStart":false});
            var Q2;
            Q2=makeQuery(id+"F1.opExtrude","CAP_EDGE",EDGE,{"disambiguationData":[OSD([sQuery(id+"F0.wireOp",EDGE,"E11.MirrorCS")])],"isStart":false});
            var Q3;
            Q3=makeQuery(id+"F1.opExtrude","CAP_EDGE",EDGE,{"disambiguationData":[OSD([sQuery(id+"F0.wireOp",EDGE,"E12.MirrorCS")])],"isStart":true});
            var Q4;
            Q4=makeQuery(id+"F1.opExtrude","CAP_EDGE",EDGE,{"disambiguationData":[OSD([sQuery(id+"F0.wireOp",EDGE,"E2")])],"isStart":false});
            var Q5;
            Q5=makeQuery(id+"F1.opExtrude","CAP_EDGE",EDGE,{"disambiguationData":[OSD([sQuery(id+"F0.wireOp",EDGE,"E4")])],"isStart":false});
            var Q6;
            Q6=makeQuery(id+"F1.opExtrude","CAP_EDGE",EDGE,{"disambiguationData":[OSD([sQuery(id+"F0.wireOp",EDGE,"E6")])],"isStart":false});
            var Q7;
            Q7=makeQuery(id+"F1.opExtrude","CAP_EDGE",EDGE,{"disambiguationData":[OSD([sQuery(id+"F0.wireOp",EDGE,"E5")])],"isStart":false});
            var Q8;
            Q8=makeQuery(id+"F1.opExtrude","CAP_EDGE",EDGE,{"disambiguationData":[OSD([sQuery(id+"F0.wireOp",EDGE,"E3")])],"isStart":false});
            var Q9;
            Q9=makeQuery(id+"F1.opExtrude","CAP_EDGE",EDGE,{"disambiguationData":[OSD([sQuery(id+"F0.wireOp",EDGE,"E12.MirrorCS")])],"isStart":false});
            var Q10;
            Q10=makeQuery(id+"F1.opExtrude","CAP_EDGE",EDGE,{"disambiguationData":[OSD([sQuery(id+"F0.wireOp",EDGE,"E13.MirrorCS")])],"isStart":false});
            var Q11;
            Q11=makeQuery(id+"F1.opExtrude","CAP_EDGE",EDGE,{"disambiguationData":[OSD([sQuery(id+"F0.wireOp",EDGE,"E14.MirrorCS")])],"isStart":false});
            var Q12;
            Q12=makeQuery(id+"F1.opExtrude","CAP_EDGE",EDGE,{"disambiguationData":[OSD([sQuery(id+"F0.wireOp",EDGE,"E15.MirrorCS")])],"isStart":false});
            var Q13;
            Q13=makeQuery(id+"F1.opExtrude","CAP_EDGE",EDGE,{"disambiguationData":[OSD([sQuery(id+"F0.wireOp",EDGE,"E16.MirrorCS")])],"isStart":false});
            var Q14;
            Q14=makeQuery(id+"F1.opExtrude","CAP_EDGE",EDGE,{"disambiguationData":[OSD([sQuery(id+"F0.wireOp",EDGE,"E10.MirrorCS")])],"isStart":true});
            var Q15;
            Q15=makeQuery(id+"F1.opExtrude","CAP_EDGE",EDGE,{"disambiguationData":[OSD([sQuery(id+"F0.wireOp",EDGE,"E0")])],"isStart":true});
            var Q16;
            Q16=makeQuery(id+"F1.opExtrude","CAP_EDGE",EDGE,{"disambiguationData":[OSD([sQuery(id+"F0.wireOp",EDGE,"E1")])],"isStart":true});
            var Q17;
            Q17=makeQuery(id+"F1.opExtrude","CAP_EDGE",EDGE,{"disambiguationData":[OSD([sQuery(id+"F0.wireOp",EDGE,"E2")])],"isStart":true});
            var Q18;
            Q18=makeQuery(id+"F1.opExtrude","CAP_EDGE",EDGE,{"disambiguationData":[OSD([sQuery(id+"F0.wireOp",EDGE,"E3")])],"isStart":true});
            var Q19;
            Q19=makeQuery(id+"F1.opExtrude","CAP_EDGE",EDGE,{"disambiguationData":[OSD([sQuery(id+"F0.wireOp",EDGE,"E4")])],"isStart":true});
            var Q20;
            Q20=makeQuery(id+"F1.opExtrude","CAP_EDGE",EDGE,{"disambiguationData":[OSD([sQuery(id+"F0.wireOp",EDGE,"E5")])],"isStart":true});
            var Q21;
            Q21=makeQuery(id+"F1.opExtrude","CAP_EDGE",EDGE,{"disambiguationData":[OSD([sQuery(id+"F0.wireOp",EDGE,"E6")])],"isStart":true});
            var Q22;
            Q22=makeQuery(id+"F1.opExtrude","CAP_EDGE",EDGE,{"disambiguationData":[OSD([sQuery(id+"F0.wireOp",EDGE,"E11.MirrorCS")])],"isStart":true});
            var Q23;
            Q23=makeQuery(id+"F1.opExtrude","CAP_EDGE",EDGE,{"disambiguationData":[OSD([sQuery(id+"F0.wireOp",EDGE,"E13.MirrorCS")])],"isStart":true});
            var Q24;
            Q24=makeQuery(id+"F1.opExtrude","CAP_EDGE",EDGE,{"disambiguationData":[OSD([sQuery(id+"F0.wireOp",EDGE,"E14.MirrorCS")])],"isStart":true});
            var Q25;
            Q25=makeQuery(id+"F1.opExtrude","CAP_EDGE",EDGE,{"disambiguationData":[OSD([sQuery(id+"F0.wireOp",EDGE,"E15.MirrorCS")])],"isStart":true});
            var Q26;
            Q26=makeQuery(id+"F1.opExtrude","CAP_EDGE",EDGE,{"disambiguationData":[OSD([sQuery(id+"F0.wireOp",EDGE,"E16.MirrorCS")])],"isStart":true});
            chamfer(context, id + "F7", {"entities" : qUnion([Q0, Q1, Q2, Q3, Q4, Q5, Q6, Q7, Q8, Q9, Q10, Q11, Q12, Q13, Q14, Q15, Q16, Q17, Q18, Q19, Q20, Q21, Q22, Q23, Q24, Q25, Q26]), "width" : 1 * mm, "tangentPropagation" : true});
        }
        {
            var Q0;
            Q0=makeQuery(id+"F1.opExtrude","CAP_EDGE",EDGE,{"disambiguationData":[OSD([sQuery(id+"F0.wireOp",EDGE,"E8")])],"isStart":false});
            var Q1;
            Q1=makeQuery(id+"F1.opExtrude","CAP_EDGE",EDGE,{"disambiguationData":[OSD([sQuery(id+"F0.wireOp",EDGE,"E8")])],"isStart":true});
            var Q2;
            Q2=makeQuery(id+"F1.opExtrude","CAP_EDGE",EDGE,{"disambiguationData":[OSD([sQuery(id+"F0.wireOp",EDGE,"E18.MirrorCS")])],"isStart":false});
            var Q3;
            Q3=makeQuery(id+"F1.opExtrude","CAP_EDGE",EDGE,{"disambiguationData":[OSD([sQuery(id+"F0.wireOp",EDGE,"E18.MirrorCS")])],"isStart":true});
            chamfer(context, id + "F8", {"entities" : qUnion([Q0, Q1, Q2, Q3]), "width" : 1 * mm, "tangentPropagation" : true});
        }
    });
